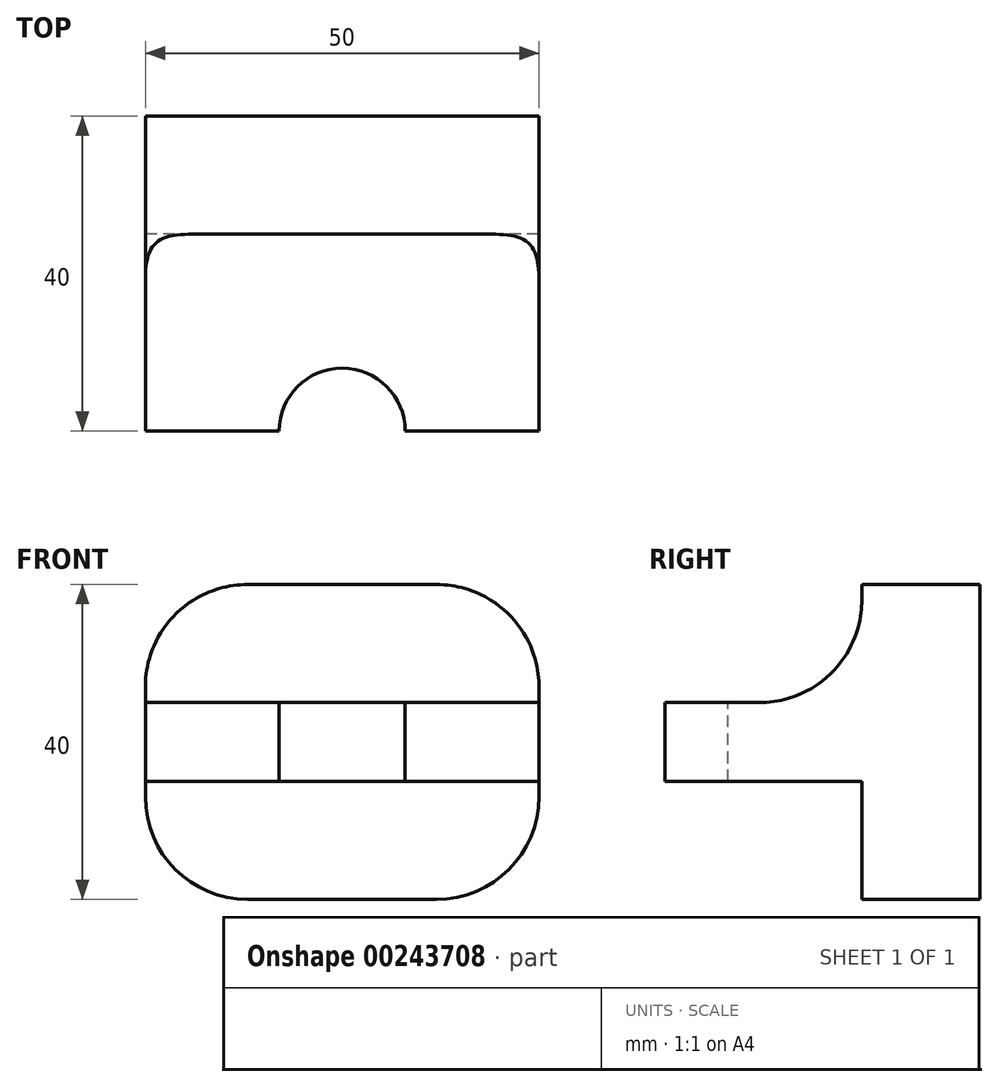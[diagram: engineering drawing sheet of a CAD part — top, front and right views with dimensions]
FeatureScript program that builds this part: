
annotation { "Feature Type Name" : "Feature", "Feature Type Description" : "" }
export const myFeature = defineFeature(function(context is Context, id is Id, definition is map)
    precondition{}
    {
        {
            var Q0;
            Q0=qCreatedBy(makeId("Front.planeOp"),FACE);
            var sketch = newSketch(context, id + "F0", { "sketchPlane" : qUnion([Q0])});
            skLineSegment(sketch, "E0.bottom", {"start": v(-25, 0) * mm, "end": v(25, 0) * mm});
            skLineSegment(sketch, "E0.top", {"start": v(-25, -10) * mm, "end": v(25, -10) * mm});
            skLineSegment(sketch, "E0.left", {"start": v(-25, 0) * mm, "end": v(-25, -10) * mm});
            skLineSegment(sketch, "E0.right", {"start": v(25, 0) * mm, "end": v(25, -10) * mm});
            skSolve(sketch);
        }
        {
            var Q0;
            Q0=makeQuery(id+"F0.imprint","IMPRINT",FACE,{"disambiguationData":[TD([[makeQuery(id+"F0.imprint","IMPRINT",EDGE,{"derivedFrom":sQuery(id+"F0.wireOp",EDGE,"E0.bottom")}),-1.0]])]});
            extrude(context, id + "F1", {"entities" : qUnion([Q0]), "oppositeDirection" : true, "depth" : 25 * mm});
        }
        {
            var Q0;
            Q0=qCreatedBy(makeId("Top.planeOp"),FACE);
            var sketch = newSketch(context, id + "F2", { "sketchPlane" : qUnion([Q0])});
            skLineSegment(sketch, "E1.bottom", {"start": v(-25, 25) * mm, "end": v(25, 25) * mm});
            skLineSegment(sketch, "E1.top", {"start": v(-25, 40) * mm, "end": v(25, 40) * mm});
            skLineSegment(sketch, "E1.left", {"start": v(-25, 25) * mm, "end": v(-25, 40) * mm});
            skLineSegment(sketch, "E1.right", {"start": v(25, 25) * mm, "end": v(25, 40) * mm});
            skSolve(sketch);
        }
        {
            var Q0;
            Q0=makeQuery(id+"F2.imprint","IMPRINT",FACE,{"disambiguationData":[TD([[makeQuery(id+"F2.imprint","IMPRINT",EDGE,{"derivedFrom":sQuery(id+"F2.wireOp",EDGE,"E1.bottom")}),1.0]])]});
            extrude(context, id + "F3", {"entities" : qUnion([Q0]), "operationType" : NewBodyOperationType.ADD, "depth" : 15 * mm, "hasSecondDirection" : true, "secondDirectionOppositeDirection" : true, "secondDirectionDepth" : 25 * mm});
        }
        {
            var Q0;
            Q0=makeQuery(id+"F1.opExtrude","SWEPT_FACE",FACE,{"disambiguationData":[OSD([sQuery(id+"F0.wireOp",EDGE,"E0.bottom")])]});
            var sketch = newSketch(context, id + "F4", { "sketchPlane" : qUnion([Q0])});
            skCircle(sketch, "E2", {"center": v(0, 0) * mm, "radius": 8 * mm});
            skSolve(sketch);
        }
        {
            var Q0;
            {var subQ0=sQuery(id+"F4.wireOp",EDGE,"E2");var subQ1=makeQuery(id+"F1.opExtrude","CAP_EDGE",EDGE,{"disambiguationData":[OSD([sQuery(id+"F0.wireOp",EDGE,"E0.bottom")])],"isStart":true});var subQ2=makeQuery(id+"F4.imprint","INTERSECT",VERTEX,{"disambiguationData":[OD(0.0)],"derivedFrom":[subQ1,subQ0]});Q0=makeQuery(id+"F4.imprint","IMPRINT",FACE,{"disambiguationData":[TD([[makeQuery(id+"F4.imprint","IMPRINT",EDGE,{"disambiguationData":[TD([[subQ2,1.0]])],"derivedFrom":subQ0}),1.0]])]});}
            extrude(context, id + "F5", {"entities" : qUnion([Q0]), "operationType" : NewBodyOperationType.REMOVE, "oppositeDirection" : true, "depth" : 25 * mm});
        }
        {
            var Q0;
            Q0=makeQuery(id+"F3.opExtrude","CAP_EDGE",EDGE,{"disambiguationData":[OSD([sQuery(id+"F2.wireOp",EDGE,"E1.left")])],"isStart":false});
            var Q1;
            Q1=makeQuery(id+"F3.opExtrude","CAP_EDGE",EDGE,{"disambiguationData":[OSD([sQuery(id+"F2.wireOp",EDGE,"E1.right")])],"isStart":false});
            var Q2;
            Q2=makeQuery(id+"F3.opExtrude","CAP_EDGE",EDGE,{"disambiguationData":[OSD([sQuery(id+"F2.wireOp",EDGE,"E1.right")])],"isStart":true});
            var Q3;
            Q3=makeQuery(id+"F3.opExtrude","CAP_EDGE",EDGE,{"disambiguationData":[OSD([sQuery(id+"F2.wireOp",EDGE,"E1.left")])],"isStart":true});
            fillet(context, id + "F6", {"entities" : qUnion([Q0, Q1, Q2, Q3]), "radius" : 13 * mm, "tangentPropagation" : true, "allowEdgeOverflow" : false});
        }
        {
            var Q0;
            Q0=makeQuery(id+"F1.opExtrude","CAP_EDGE",EDGE,{"disambiguationData":[OSD([sQuery(id+"F0.wireOp",EDGE,"E0.bottom")])],"isStart":false});
            var Q1;
            Q1=makeQuery(id+"F1.opExtrude","CAP_EDGE",EDGE,{"disambiguationData":[OSD([sQuery(id+"F0.wireOp",EDGE,"E0.top")])],"isStart":false});
            fillet(context, id + "F7", {"entities" : qUnion([Q0, Q1]), "radius" : 13 * mm, "tangentPropagation" : true, "allowEdgeOverflow" : false});
        }
    });
